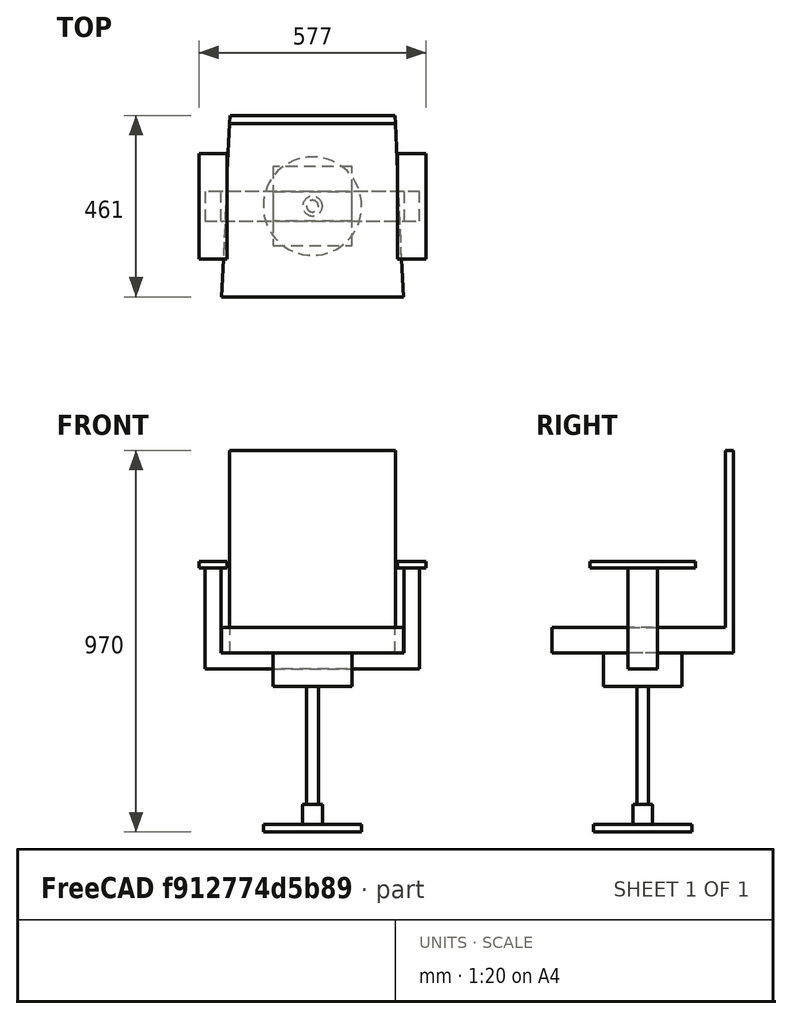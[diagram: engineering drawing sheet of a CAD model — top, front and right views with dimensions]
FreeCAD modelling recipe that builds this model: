
FCSTD DOCUMENT  (FreeCAD 1.0R39109 (Git))
Label: chair02_00503
License: All rights reserved
LicenseURL: https://en.wikipedia.org/wiki/All_rights_reserved
objects: TechDraw::DrawViewDimension×13, Sketcher::SketchObject×10, PartDesign::Pad×10, TechDraw::DrawViewAnnotation×9, PartDesign::Body×5, PartDesign::ShapeBinder×4, TechDraw::DrawSVGTemplate×3, TechDraw::DrawProjGroupItem×3, TechDraw::DrawPage×3, TechDraw::DrawViewSection×3, App::Part×1
note: 85 computed .brp shape members not serialized (recipe doc carries the construction recipe); baked Part::Feature solids carry a one-line shape summary decoded from their .brp

FEATURE [Sketcher::SketchObject] Sketch
  ArcFitTolerance = 1e-06
  AttachmentSupport = -> [XY_Plane]
  FullyConstrained = true
  MakeInternals = false
  MapMode = 5
  sketch-geometry (1):
    g0: Circle CenterX=0 CenterY=0 CenterZ=0 NormalX=0 NormalY=0 NormalZ=1 AngleXU=0 Radius=125
  constraints (2):
    c: Diameter(g0) = 250
    c: Coincident(g0,g-1)
FEATURE [PartDesign::Pad] Pad
  Direction = (0,0,1)
  Length = 20
  Length2 = 10
  Profile = -> Sketch
  ReferenceAxis = -> Sketch [N_Axis]
  Refine = true
  Suppressed = false
  Type = 0
FEATURE [Sketcher::SketchObject] Sketch001
  ArcFitTolerance = 1e-06
  AttachmentSupport = -> [Pad]
  FullyConstrained = true
  MakeInternals = false
  MapMode = 5
  Placement = pos=(0,0,20) rot=(0,0,1;0rad)
  sketch-geometry (1):
    g0: Circle CenterX=0 CenterY=0 CenterZ=0 NormalX=0 NormalY=0 NormalZ=1 AngleXU=0 Radius=25
  constraints (2):
    c: Diameter(g0) = 50
    c: Coincident(g0,g-1)
FEATURE [PartDesign::Pad] Pad001
  BaseFeature = -> Pad
  Direction = (0,0,1)
  Length = 50
  Length2 = 10
  Profile = -> Sketch001
  ReferenceAxis = -> Sketch001 [N_Axis]
  Refine = true
  Suppressed = false
  Type = 0
FEATURE [PartDesign::Body] Body  label="Body1"
  AllowCompound = false
  Group = -> [Sketch,Pad,Sketch001,Pad001]
  Origin = -> Origin
  Tip = -> Pad001
FEATURE [PartDesign::ShapeBinder] CopyPad001  label="Body2_Sketch_P.lane"
  Placement = pos=(0,0,50) rot=(0,0,1;0rad)
  TraceSupport = false
FEATURE [Sketcher::SketchObject] Sketch002
  ArcFitTolerance = 1e-06
  AttachmentSupport = -> [CopyPad001]
  FullyConstrained = true
  MakeInternals = false
  MapMode = 5
  Placement = pos=(0,0,70) rot=(0,0,1;0rad)
  sketch-geometry (1):
    g0: Circle CenterX=0 CenterY=0 CenterZ=0 NormalX=0 NormalY=0 NormalZ=1 AngleXU=0 Radius=15
  constraints (2):
    c: Diameter(g0) = 30
    c: Coincident(g0,g-1)
FEATURE [PartDesign::Pad] Pad002
  Direction = (0,0,1)
  Length = 300
  Length2 = 10
  Placement = pos=(0,0,50) rot=(0,0,1;0rad)
  Profile = -> Sketch002
  ReferenceAxis = -> Sketch002 [N_Axis]
  Refine = true
  Suppressed = false
  Type = 0
FEATURE [PartDesign::Body] Body001  label="Body2"
  AllowCompound = false
  Group = -> [CopyPad001,Sketch002,Pad002]
  Origin = -> Origin001
  Tip = -> Pad002
FEATURE [PartDesign::ShapeBinder] CopyPad002  label="Body3_Sketch_Plane"
  Placement = pos=(0,0,300) rot=(0,0,1;0rad)
  TraceSupport = false
FEATURE [Sketcher::SketchObject] Sketch003
  ArcFitTolerance = 1e-06
  AttachmentSupport = -> [CopyPad002]
  FullyConstrained = true
  MakeInternals = false
  MapMode = 5
  Placement = pos=(0,0,370) rot=(0,0,1;0rad)
  sketch-geometry (5):
    g0: LineSegment StartX=-100 StartY=-100 StartZ=0 EndX=100 EndY=-100 EndZ=0
    g1: LineSegment StartX=100 StartY=-100 StartZ=0 EndX=100 EndY=100 EndZ=0
    g2: LineSegment StartX=100 StartY=100 StartZ=0 EndX=-100 EndY=100 EndZ=0
    g3: LineSegment StartX=-100 StartY=100 StartZ=0 EndX=-100 EndY=-100 EndZ=0
    g4: GeomPoint [constr] X=0 Y=0 Z=0
  constraints (12):
    c: Coincident(g0,g1)
    c: Coincident(g1,g2)
    c: Coincident(g2,g3)
    c: Coincident(g3,g0)
    c: Horizontal(g0)
    c: Horizontal(g2)
    c: Vertical(g1)
    c: Vertical(g3)
    c: Symmetric(g2,g0,g4)
    c: Distance(g1,g3) = 200
    c: Distance(g0,g2) = 200
    c: Coincident(g4,g-1)
FEATURE [PartDesign::Pad] Pad003
  Direction = (0,0,1)
  Length = 45
  Length2 = 10
  Placement = pos=(0,0,300) rot=(0,0,1;0rad)
  Profile = -> Sketch003
  ReferenceAxis = -> Sketch003 [N_Axis]
  Refine = true
  Suppressed = false
  Type = 0
FEATURE [PartDesign::ShapeBinder] CopyPad003  label="Body4_Sketch_Plane"
  Placement = pos=(0,0,45) rot=(0,0,1;0rad)
  TraceSupport = false
FEATURE [Sketcher::SketchObject] Sketch004
  ArcFitTolerance = 1e-06
  AttachmentSupport = -> [CopyPad003]
  FullyConstrained = true
  MakeInternals = false
  MapMode = 5
  Placement = pos=(0,0,415) rot=(0,0,1;0rad)
  sketch-geometry (5):
    g0: LineSegment StartX=-272.5 StartY=-37.5 StartZ=0 EndX=272.5 EndY=-37.5 EndZ=0
    g1: LineSegment StartX=272.5 StartY=-37.5 StartZ=0 EndX=272.5 EndY=37.5 EndZ=0
    g2: LineSegment StartX=272.5 StartY=37.5 StartZ=0 EndX=-272.5 EndY=37.5 EndZ=0
    g3: LineSegment StartX=-272.5 StartY=37.5 StartZ=0 EndX=-272.5 EndY=-37.5 EndZ=0
    g4: GeomPoint [constr] X=0 Y=0 Z=0
  constraints (12):
    c: Coincident(g0,g1)
    c: Coincident(g1,g2)
    c: Coincident(g2,g3)
    c: Coincident(g3,g0)
    c: Horizontal(g0)
    c: Horizontal(g2)
    c: Vertical(g1)
    c: Vertical(g3)
    c: Symmetric(g2,g0,g4)
    c: Distance(g1,g3) = 545
    c: Distance(g0,g2) = 75
    c: Coincident(g4,g-1)
FEATURE [PartDesign::Pad] Pad004
  Direction = (0,0,1)
  Length = 40
  Length2 = 10
  Placement = pos=(0,0,45) rot=(0,0,1;0rad)
  Profile = -> Sketch004
  ReferenceAxis = -> Sketch004 [N_Axis]
  Refine = true
  Suppressed = false
  Type = 0
FEATURE [Sketcher::SketchObject] Sketch005
  ArcFitTolerance = 1e-06
  AttachmentSupport = -> [Pad004]
  ExternalGeometry = -> [Pad004]
  FullyConstrained = true
  MakeInternals = false
  MapMode = 5
  Placement = pos=(0,0,455) rot=(0,0,1;0rad)
  sketch-geometry (8):
    g0: LineSegment StartX=-272.5 StartY=37.5 StartZ=0 EndX=-272.5 EndY=-37.5 EndZ=0
    g1: LineSegment StartX=-272.5 StartY=-37.5 StartZ=0 EndX=-232.5 EndY=-37.5 EndZ=0
    g2: LineSegment StartX=-232.5 StartY=-37.5 StartZ=0 EndX=-232.5 EndY=37.5 EndZ=0
    g3: LineSegment StartX=-232.5 StartY=37.5 StartZ=0 EndX=-272.5 EndY=37.5 EndZ=0
    g4: LineSegment StartX=272.5 StartY=37.5 StartZ=0 EndX=232.5 EndY=37.5 EndZ=0
    g5: LineSegment StartX=232.5 StartY=37.5 StartZ=0 EndX=232.5 EndY=-37.5 EndZ=0
    g6: LineSegment StartX=232.5 StartY=-37.5 StartZ=0 EndX=272.5 EndY=-37.5 EndZ=0
    g7: LineSegment StartX=272.5 StartY=-37.5 StartZ=0 EndX=272.5 EndY=37.5 EndZ=0
  constraints (22):
    c: Coincident(g0,g1)
    c: Coincident(g1,g2)
    c: Coincident(g2,g3)
    c: Coincident(g3,g0)
    c: Vertical(g0)
    c: Vertical(g2)
    c: Horizontal(g1)
    c: Horizontal(g3)
    c: Coincident(g0,g-3)
    c: PointOnObject(g1,g-4)
    c: DistanceX(g3,g3) = 40
    c: Coincident(g4,g5)
    c: Coincident(g5,g6)
    c: Coincident(g6,g7)
    c: Coincident(g7,g4)
    c: Horizontal(g4)
    c: Horizontal(g6)
    c: Vertical(g5)
    c: Vertical(g7)
    c: Coincident(g4,g-3)
    c: PointOnObject(g5,g-4)
    c: Equal(g4,g3)
FEATURE [PartDesign::Pad] Pad005
  BaseFeature = -> Pad004
  Direction = (0,0,1)
  Length = 216
  Length2 = 10
  Placement = pos=(0,0,45) rot=(0,0,1;0rad)
  Profile = -> Sketch005
  ReferenceAxis = -> Sketch005 [N_Axis]
  Refine = true
  Suppressed = false
  Type = 0
FEATURE [Sketcher::SketchObject] Sketch006
  ArcFitTolerance = 1e-06
  AttachmentSupport = -> [Pad005]
  ExternalGeometry = -> [Pad005]
  FullyConstrained = true
  MakeInternals = false
  MapMode = 5
  Placement = pos=(0,0,671) rot=(0,0,1;0rad)
  sketch-geometry (16):
    g0: LineSegment StartX=-288.5 StartY=134 StartZ=0 EndX=-288.5 EndY=-134 EndZ=0
    g1: LineSegment StartX=-288.5 StartY=-134 StartZ=0 EndX=-216.5 EndY=-134 EndZ=0
    g2: LineSegment StartX=-216.5 StartY=-134 StartZ=0 EndX=-216.5 EndY=134 EndZ=0
    g3: LineSegment StartX=-216.5 StartY=134 StartZ=0 EndX=-288.5 EndY=134 EndZ=0
    g4: LineSegment StartX=216.5 StartY=134 StartZ=0 EndX=216.5 EndY=-134 EndZ=0
    g5: LineSegment StartX=216.5 StartY=-134 StartZ=0 EndX=288.5 EndY=-134 EndZ=0
    g6: LineSegment StartX=288.5 StartY=-134 StartZ=0 EndX=288.5 EndY=134 EndZ=0
    g7: LineSegment StartX=288.5 StartY=134 StartZ=0 EndX=216.5 EndY=134 EndZ=0
    g8: LineSegment [constr] StartX=-272.5 StartY=37.5 StartZ=0 EndX=-232.5 EndY=-37.5 EndZ=0
    g9: LineSegment [constr] StartX=-252.5 StartY=0 StartZ=0 EndX=-272.5 EndY=-37.5 EndZ=0
    g10: LineSegment [constr] StartX=232.5 StartY=37.5 StartZ=0 EndX=272.5 EndY=-37.5 EndZ=0
    g11: LineSegment [constr] StartX=272.5 StartY=37.5 StartZ=0 EndX=252.5 EndY=0 EndZ=0
    g12: LineSegment [constr] StartX=-216.5 StartY=134 StartZ=0 EndX=-288.5 EndY=-134 EndZ=0
    g13: LineSegment [constr] StartX=-288.5 StartY=134 StartZ=0 EndX=-252.5 EndY=0 EndZ=0
    g14: LineSegment [constr] StartX=216.5 StartY=134 StartZ=0 EndX=288.5 EndY=-134 EndZ=0
    g15: LineSegment [constr] StartX=288.5 StartY=134 StartZ=0 EndX=252.5 EndY=0 EndZ=0
  constraints (38):
    c: Coincident(g0,g1)
    c: Coincident(g1,g2)
    c: Coincident(g2,g3)
    c: Coincident(g3,g0)
    c: Vertical(g0)
    c: Vertical(g2)
    c: Horizontal(g1)
    c: Horizontal(g3)
    c: Coincident(g4,g5)
    c: Coincident(g5,g6)
    c: Coincident(g6,g7)
    c: Coincident(g7,g4)
    c: Vertical(g4)
    c: Vertical(g6)
    c: Horizontal(g5)
    c: Horizontal(g7)
    c: Equal(g7,g3)
    c: Equal(g2,g4)
    c: DistanceX(g3,g3) = 72
    c: Coincident(g8,g-4)
    c: Coincident(g8,g-3)
    c: Coincident(g9,g-4)
    c: Coincident(g10,g-5)
    c: Coincident(g10,g-6)
    c: Coincident(g11,g-6)
    c: Symmetric(g10,g10,g11)
    c: Symmetric(g8,g8,g9)
    c: Coincident(g12,g2)
    c: Coincident(g12,g0)
    c: Coincident(g13,g0)
    c: Symmetric(g12,g12,g13)
    c: Coincident(g9,g13)
    c: Coincident(g14,g4)
    c: Coincident(g14,g5)
    c: Coincident(g15,g6)
    c: Symmetric(g14,g14,g15)
    c: Coincident(g15,g11)
    c: DistanceY(g2,g2) = 268
FEATURE [PartDesign::Pad] Pad006
  BaseFeature = -> Pad005
  Direction = (0,0,1)
  Length = 17
  Length2 = 10
  Placement = pos=(0,0,45) rot=(0,0,1;0rad)
  Profile = -> Sketch006
  ReferenceAxis = -> Sketch006 [N_Axis]
  Refine = true
  Suppressed = false
  Type = 0
FEATURE [PartDesign::Body] Body003  label="Body4"
  AllowCompound = false
  Group = -> [CopyPad003,Sketch004,Pad004,Sketch005,Pad005,Sketch006,Pad006]
  Origin = -> Origin003
  Tip = -> Pad006
FEATURE [PartDesign::ShapeBinder] CopyPad006  label="Body5_Sketch_Plane"
  Placement = pos=(0,0,45) rot=(0,0,1;0rad)
  TraceSupport = false
FEATURE [Sketcher::SketchObject] Sketch009
  ArcFitTolerance = 1e-06
  AttachmentSupport = -> [Pad003]
  ExternalGeometry = -> [Pad003]
  FullyConstrained = true
  MakeInternals = false
  MapMode = 5
  Placement = pos=(0,0,415) rot=(0,0,1;0rad)
  sketch-geometry (8):
    g0: LineSegment StartX=-100 StartY=100 StartZ=0 EndX=-100 EndY=37.5 EndZ=0
    g1: LineSegment StartX=-100 StartY=37.5 StartZ=0 EndX=100 EndY=37.5 EndZ=0
    g2: LineSegment StartX=100 StartY=37.5 StartZ=0 EndX=100 EndY=100 EndZ=0
    g3: LineSegment StartX=100 StartY=100 StartZ=0 EndX=-100 EndY=100 EndZ=0
    g4: LineSegment StartX=100 StartY=-100 StartZ=0 EndX=100 EndY=-37.5 EndZ=0
    g5: LineSegment StartX=100 StartY=-37.5 StartZ=0 EndX=-100 EndY=-37.5 EndZ=0
    g6: LineSegment StartX=-100 StartY=-37.5 StartZ=0 EndX=-100 EndY=-100 EndZ=0
    g7: LineSegment StartX=-100 StartY=-100 StartZ=0 EndX=100 EndY=-100 EndZ=0
  constraints (21):
    c: Coincident(g0,g1)
    c: Coincident(g1,g2)
    c: Coincident(g2,g3)
    c: Coincident(g3,g0)
    c: Vertical(g0)
    c: Vertical(g2)
    c: Horizontal(g1)
    c: Horizontal(g3)
    c: Coincident(g0,g-3)
    c: PointOnObject(g1,g-4)
    c: Coincident(g4,g5)
    c: Coincident(g5,g6)
    c: Coincident(g6,g7)
    c: Coincident(g7,g4)
    c: Vertical(g6)
    c: Horizontal(g5)
    c: Horizontal(g7)
    c: Coincident(g4,g-4)
    c: PointOnObject(g5,g-3)
    c: DistanceY(g4,g1) = 75
    c: Symmetric(g1,g4,g-1)
FEATURE [PartDesign::Pad] Pad009
  BaseFeature = -> Pad003
  Direction = (0,0,1)
  Length = 40
  Length2 = 10
  Placement = pos=(0,0,300) rot=(0,0,1;0rad)
  Profile = -> Sketch009
  ReferenceAxis = -> Sketch009 [N_Axis]
  Refine = true
  Suppressed = false
  Type = 0
FEATURE [PartDesign::Body] Body002  label="Body3"
  AllowCompound = false
  Group = -> [CopyPad002,Sketch003,Pad003,Sketch009,Pad009]
  Origin = -> Origin002
  Tip = -> Pad009
FEATURE [Sketcher::SketchObject] Sketch007
  ArcFitTolerance = 1e-06
  AttachmentSupport = -> [CopyPad006]
  FullyConstrained = true
  MakeInternals = false
  MapMode = 5
  Placement = pos=(0,0,455) rot=(0,0,1;0rad)
  sketch-geometry (8):
    g0: LineSegment StartX=-210 StartY=230.5 StartZ=0 EndX=-231 EndY=-230.5 EndZ=0
    g1: LineSegment StartX=-231 StartY=-230.5 StartZ=0 EndX=231 EndY=-230.5 EndZ=0
    g2: LineSegment StartX=231 StartY=-230.5 StartZ=0 EndX=210 EndY=230.5 EndZ=0
    g3: LineSegment StartX=210 StartY=230.5 StartZ=0 EndX=-210 EndY=230.5 EndZ=0
    g4: LineSegment [constr] StartX=210 StartY=230.5 StartZ=0 EndX=2.84e-14 EndY=0 EndZ=0
    g5: LineSegment [constr] StartX=2.84e-14 StartY=0 StartZ=0 EndX=-210 EndY=230.5 EndZ=0
    g6: LineSegment [constr] StartX=210 StartY=230.5 StartZ=0 EndX=210 EndY=0 EndZ=0
    g7: LineSegment [constr] StartX=231 StartY=-230.5 StartZ=0 EndX=231 EndY=0 EndZ=0
  constraints (20):
    c: Coincident(g2,g1)
    c: DistanceX(g1,g1) = 462
    c: DistanceX(g3,g3) = 420
    c: Coincident(g1,g0)
    c: Symmetric(g2,g0,g-2)
    c: Coincident(g2,g3)
    c: Coincident(g3,g0)
    c: Coincident(g4,g2)
    c: Coincident(g4,g-1)
    c: Coincident(g5,g4)
    c: Coincident(g5,g0)
    c: DistanceY(g2,g2) = 461
    c: Coincident(g6,g2)
    c: PointOnObject(g6,g-1)
    c: Vertical(g6)
    c: Coincident(g7,g1)
    c: PointOnObject(g7,g-1)
    c: Vertical(g7)
    c: Equal(g7,g6)
    c: Symmetric(g1,g0,g-2)
FEATURE [PartDesign::Pad] Pad007
  Direction = (0,0,1)
  Length = 65
  Length2 = 10
  Placement = pos=(0,0,45) rot=(0,0,1;0rad)
  Profile = -> Sketch007
  ReferenceAxis = -> Sketch007 [N_Axis]
  Refine = true
  Suppressed = false
  Type = 0
FEATURE [Sketcher::SketchObject] Sketch008
  ArcFitTolerance = 1e-06
  AttachmentSupport = -> [Pad007]
  ExternalGeometry = -> [Pad007]
  FullyConstrained = true
  MakeInternals = false
  MapMode = 5
  Placement = pos=(0,0,520) rot=(0,0,1;0rad)
  sketch-geometry (4):
    g0: LineSegment StartX=-210 StartY=230.5 StartZ=0 EndX=210 EndY=230.5 EndZ=0
    g1: LineSegment StartX=-210 StartY=230.5 StartZ=0 EndX=-210.957 EndY=209.5 EndZ=0
    g2: LineSegment StartX=-210.957 StartY=209.5 StartZ=0 EndX=210.957 EndY=209.5 EndZ=0
    g3: LineSegment StartX=210 StartY=230.5 StartZ=0 EndX=210.957 EndY=209.5 EndZ=0
  constraints (10):
    c: Coincident(g0,g-3)
    c: Coincident(g0,g-4)
    c: Coincident(g1,g0)
    c: PointOnObject(g1,g-3)
    c: Coincident(g2,g1)
    c: PointOnObject(g2,g-4)
    c: Horizontal(g2)
    c: Coincident(g3,g0)
    c: Coincident(g3,g2)
    c: DistanceY(g1,g1) = 21
FEATURE [PartDesign::Pad] Pad008
  BaseFeature = -> Pad007
  Direction = (0,0,1)
  Length = 450
  Length2 = 10
  Placement = pos=(0,0,45) rot=(0,0,1;0rad)
  Profile = -> Sketch008
  ReferenceAxis = -> Sketch008 [N_Axis]
  Refine = true
  Suppressed = false
  Type = 0
FEATURE [PartDesign::Body] Body004  label="Body5"
  AllowCompound = false
  Group = -> [CopyPad006,Sketch007,Pad007,Sketch008,Pad008]
  Origin = -> Origin004
  Tip = -> Pad008
FEATURE [App::Part] Part  label="chair02"
  Group = -> [Body,Body001,Body002,Body003,Body004]
  Origin = -> Origin005
FEATURE [TechDraw::DrawSVGTemplate] Template  label="テンプレート"
  Height = 210
  Orientation = 1
  Template = <userpath>/AppData/Local/Programs/FreeCAD 1.0/data/Mod/TechDraw/Templates/A4_Landscape_blank.svg
  Width = 297
FEATURE [TechDraw::DrawProjGroupItem] View
  CoarseView = false
  Direction = (0,0,1)
  Focus = 100
  HardHidden = true
  IsoCount = 0
  IsoHidden = false
  IsoVisible = false
  LockPosition = false
  Perspective = false
  Rotation = 0
  RotationVector = (1,0,0)
  Scale = 0.333333
  ScaleType = 2
  ScrubCount = 1
  SeamHidden = false
  SeamVisible = false
  SmoothHidden = false
  SmoothVisible = true
  Source = -> [Part]
  Type = 0
  X = 131.425
  XDirection = (1,0,0)
  Y = 107.897
FEATURE [TechDraw::DrawViewDimension] Dimension  label="寸法"
  AngleOverride = false
  Arbitrary = false
  ArbitraryTolerances = false
  BoxCorners = (2) [(-96.1666,-76.8333,0),(96.1666,76.8333,0)]
  EqualTolerance = true
  ExtensionAngle = 0
  FormatSpec = %.2w
  FormatSpecOverTolerance = %+.2w
  FormatSpecUnderTolerance = %+.2w
  Inverted = false
  LineAngle = 0
  LockPosition = false
  MeasureType = 1
  OverTolerance = 0
  References2D = -> [View]
  Rotation = 0
  Scale = 0.2
  ScaleType = 2
  TheoreticalExact = false
  Type = 1
  UnderTolerance = 0
  X = 0
  Y = 93.9298
FEATURE [TechDraw::DrawViewDimension] Dimension001  label="寸法001"
  AngleOverride = false
  Arbitrary = false
  ArbitraryTolerances = false
  BoxCorners = (2) [(-96.1666,-76.8333,0),(96.1666,76.8333,0)]
  EqualTolerance = true
  ExtensionAngle = 0
  FormatSpec = %.2w
  FormatSpecOverTolerance = %+.2w
  FormatSpecUnderTolerance = %+.2w
  Inverted = false
  LineAngle = 0
  LockPosition = false
  MeasureType = 1
  OverTolerance = 0
  References2D = -> [View]
  Rotation = 0
  Scale = 0.2
  ScaleType = 2
  TheoreticalExact = false
  Type = 2
  UnderTolerance = 0
  X = 135.701
  Y = 0
FEATURE [TechDraw::DrawViewDimension] Dimension002  label="寸法002"
  AngleOverride = false
  Arbitrary = false
  ArbitraryTolerances = false
  BoxCorners = (2) [(-96.1666,-76.8333,0),(96.1666,76.8333,0)]
  EqualTolerance = true
  ExtensionAngle = 0
  FormatSpec = %.2w
  FormatSpecOverTolerance = %+.2w
  FormatSpecUnderTolerance = %+.2w
  Inverted = false
  LineAngle = 0
  LockPosition = false
  MeasureType = 1
  OverTolerance = 0
  References2D = -> [View]
  Rotation = 0
  Scale = 0.2
  ScaleType = 2
  TheoreticalExact = false
  Type = 2
  UnderTolerance = 0
  X = 113.57
  Y = 61.6706
FEATURE [TechDraw::DrawViewDimension] Dimension003  label="寸法003"
  AngleOverride = false
  Arbitrary = false
  ArbitraryTolerances = false
  BoxCorners = (2) [(-96.1666,-76.8333,0),(96.1666,76.8333,0)]
  EqualTolerance = true
  ExtensionAngle = 0
  FormatSpec = %.2w
  FormatSpecOverTolerance = %+.2w
  FormatSpecUnderTolerance = %+.2w
  Inverted = false
  LineAngle = 0
  LockPosition = false
  MeasureType = 1
  OverTolerance = 0
  References2D = -> [View]
  Rotation = 0
  Scale = 0.2
  ScaleType = 2
  TheoreticalExact = false
  Type = 2
  UnderTolerance = 0
  X = 125.233
  Y = 0.063601
FEATURE [TechDraw::DrawViewDimension] Dimension004  label="寸法004"
  AngleOverride = false
  Arbitrary = false
  ArbitraryTolerances = false
  BoxCorners = (2) [(-96.1666,-76.8333,0),(96.1666,76.8333,0)]
  EqualTolerance = true
  ExtensionAngle = 0
  FormatSpec = %.2w
  FormatSpecOverTolerance = %+.2w
  FormatSpecUnderTolerance = %+.2w
  Inverted = false
  LineAngle = 0
  LockPosition = false
  MeasureType = 1
  OverTolerance = 0
  References2D = -> [View]
  Rotation = 0
  Scale = 0.2
  ScaleType = 2
  TheoreticalExact = false
  Type = 1
  UnderTolerance = 0
  X = -84.1666
  Y = 58.5053
FEATURE [TechDraw::DrawViewDimension] Dimension005  label="寸法005"
  AngleOverride = false
  Arbitrary = false
  ArbitraryTolerances = false
  BoxCorners = (2) [(-96.1666,-76.8333,0),(96.1666,76.8333,0)]
  EqualTolerance = true
  ExtensionAngle = 0
  FormatSpec = %.2w
  FormatSpecOverTolerance = %+.2w
  FormatSpecUnderTolerance = %+.2w
  Inverted = false
  LineAngle = 0
  LockPosition = false
  MeasureType = 1
  OverTolerance = 0
  References2D = -> [View]
  Rotation = 0
  Scale = 0.2
  ScaleType = 2
  TheoreticalExact = false
  Type = 2
  UnderTolerance = 0
  X = -108.801
  Y = 0
FEATURE [TechDraw::DrawViewDimension] Dimension006  label="寸法006"
  AngleOverride = false
  Arbitrary = false
  ArbitraryTolerances = false
  BoxCorners = (2) [(-96.1666,-76.8333,0),(96.1666,76.8333,0)]
  EqualTolerance = true
  ExtensionAngle = 0
  FormatSpec = %.2w
  FormatSpecOverTolerance = %+.2w
  FormatSpecUnderTolerance = %+.2w
  Inverted = false
  LineAngle = 0
  LockPosition = false
  MeasureType = 1
  OverTolerance = 0
  References2D = -> [View]
  Rotation = 0
  Scale = 0.2
  ScaleType = 2
  TheoreticalExact = false
  Type = 1
  UnderTolerance = 0
  X = 0
  Y = -83.8244
FEATURE [TechDraw::DrawPage] Page  label="用紙"
  KeepUpdated = true
  NextBalloonIndex = 1
  ProjectionType = 0
  Template = -> Template
  Views = -> [View,Dimension,Dimension001,Dimension002,Dimension003,Dimension004,Dimension005,Dimension006]
FEATURE [TechDraw::DrawSVGTemplate] Template001  label="テンプレート001"
  Height = 210
  Orientation = 1
  Template = <userpath>/AppData/Local/Programs/FreeCAD 1.0/data/Mod/TechDraw/Templates/A4_Landscape_blank.svg
  Width = 297
FEATURE [TechDraw::DrawSVGTemplate] Template002  label="テンプレート002"
  Height = 210
  Orientation = 1
  Template = <userpath>/AppData/Local/Programs/FreeCAD 1.0/data/Mod/TechDraw/Templates/A4_Landscape_blank.svg
  Width = 297
FEATURE [TechDraw::DrawProjGroupItem] View001
  CoarseView = false
  Direction = (0,-1,0)
  Focus = 100
  HardHidden = true
  IsoCount = 0
  IsoHidden = false
  IsoVisible = false
  LockPosition = false
  Perspective = false
  Rotation = 0
  RotationVector = (1,0,0)
  Scale = 0.2
  ScaleType = 2
  ScrubCount = 1
  SeamHidden = false
  SeamVisible = false
  SmoothHidden = false
  SmoothVisible = true
  Source = -> [Part]
  Type = 0
  X = 72.2264
  XDirection = (1,0,0)
  Y = 108.632
FEATURE [TechDraw::DrawViewSection] SectionView  label="セクション  - "
  BaseView = -> View001
  CoarseView = false
  CutSurfaceDisplay = 2
  Direction = (1e-16,0,1)
  FileGeomPattern = <userpath>\AppData\Local\Programs\FreeCAD 1.0\data\Mod/TechDraw/PAT/FCPAT.pat
  FileHatchPattern = <userpath>\AppData\Local\Programs\FreeCAD 1.0\data\Mod/TechDraw/Patterns/simple.svg
  Focus = 100
  FuseBeforeCut = false
  HardHidden = true
  HatchOffset = (0,0,0)
  HatchRotation = 0
  HatchScale = 1
  IsoCount = 0
  IsoHidden = false
  IsoVisible = false
  LockPosition = false
  NameGeomPattern = Diamond
  Perspective = false
  Rotation = 0
  Scale = 0.15
  ScaleType = 2
  ScrubCount = 1
  SeamHidden = false
  SeamVisible = false
  SectionDirection = 4
  SectionLineStretch = 1
  SectionNormal = (1e-16,0,1)
  SectionOrigin = (0,0,581)
  SmoothHidden = false
  SmoothVisible = true
  Source = -> [Part]
  TrimAfterCut = false
  UsePreviousCut = false
  X = 215.858
  XDirection = (1,0,-1e-16)
  Y = 166.085
FEATURE [TechDraw::DrawViewSection] SectionView001  label="セクション001  - "
  BaseView = -> View001
  CoarseView = false
  CutSurfaceDisplay = 2
  Direction = (1e-16,0,1)
  FileGeomPattern = <userpath>\AppData\Local\Programs\FreeCAD 1.0\data\Mod/TechDraw/PAT/FCPAT.pat
  FileHatchPattern = <userpath>\AppData\Local\Programs\FreeCAD 1.0\data\Mod/TechDraw/Patterns/simple.svg
  Focus = 100
  FuseBeforeCut = false
  HardHidden = true
  HatchOffset = (0,0,0)
  HatchRotation = 0
  HatchScale = 1
  IsoCount = 0
  IsoHidden = false
  IsoVisible = false
  LockPosition = false
  NameGeomPattern = Diamond
  Perspective = false
  Rotation = 0
  Scale = 0.15
  ScaleType = 2
  ScrubCount = 1
  SeamHidden = false
  SeamVisible = false
  SectionDirection = 4
  SectionLineStretch = 1
  SectionNormal = (1e-16,0,1)
  SectionOrigin = (0,0,437)
  SmoothHidden = false
  SmoothVisible = true
  Source = -> [Part]
  TrimAfterCut = false
  UsePreviousCut = false
  X = 215.086
  XDirection = (1,0,-1e-16)
  Y = 92.3168
FEATURE [TechDraw::DrawViewSection] SectionView002  label="セクション002  - "
  BaseView = -> View001
  CoarseView = false
  CutSurfaceDisplay = 2
  Direction = (1e-16,0,1)
  FileGeomPattern = <userpath>\AppData\Local\Programs\FreeCAD 1.0\data\Mod/TechDraw/PAT/FCPAT.pat
  FileHatchPattern = <userpath>\AppData\Local\Programs\FreeCAD 1.0\data\Mod/TechDraw/Patterns/simple.svg
  Focus = 100
  FuseBeforeCut = false
  HardHidden = true
  HatchOffset = (0,0,0)
  HatchRotation = 0
  HatchScale = 1
  IsoCount = 0
  IsoHidden = false
  IsoVisible = false
  LockPosition = false
  NameGeomPattern = Diamond
  Perspective = false
  Rotation = 0
  Scale = 0.15
  ScaleType = 2
  ScrubCount = 1
  SeamHidden = false
  SeamVisible = false
  SectionDirection = 4
  SectionLineStretch = 1
  SectionNormal = (1e-16,0,1)
  SectionOrigin = (0,0,200)
  SmoothHidden = false
  SmoothVisible = true
  Source = -> [Part]
  TrimAfterCut = false
  UsePreviousCut = false
  X = 214.868
  XDirection = (1,0,-1e-16)
  Y = 24.434
FEATURE [TechDraw::DrawViewDimension] Dimension010  label="寸法010"
  AngleOverride = false
  Arbitrary = false
  ArbitraryTolerances = false
  BoxCorners = (2) [(-40.875,-18.75,0),(40.875,18.75,0)]
  EqualTolerance = true
  ExtensionAngle = 0
  FormatSpec = %.2w
  FormatSpecOverTolerance = %+.2w
  FormatSpecUnderTolerance = %+.2w
  Inverted = false
  LineAngle = 0
  LockPosition = false
  MeasureType = 1
  OverTolerance = 0
  References2D = -> [SectionView001]
  Rotation = 0
  Scale = 0.2
  ScaleType = 2
  TheoreticalExact = false
  Type = 1
  UnderTolerance = 0
  X = -23.2227
  Y = -15.8558
FEATURE [TechDraw::DrawViewDimension] Dimension011  label="寸法011"
  AngleOverride = false
  Arbitrary = false
  ArbitraryTolerances = false
  BoxCorners = (2) [(-40.875,-18.75,0),(40.875,18.75,0)]
  EqualTolerance = true
  ExtensionAngle = 0
  FormatSpec = %.2w
  FormatSpecOverTolerance = %+.2w
  FormatSpecUnderTolerance = %+.2w
  Inverted = false
  LineAngle = 0
  LockPosition = false
  MeasureType = 1
  OverTolerance = 0
  References2D = -> [SectionView001]
  Rotation = 0
  Scale = 0.2
  ScaleType = 2
  TheoreticalExact = false
  Type = 2
  UnderTolerance = 0
  X = 58.5124
  Y = 0
FEATURE [TechDraw::DrawViewDimension] Dimension016  label="寸法016"
  AngleOverride = false
  Arbitrary = false
  ArbitraryTolerances = false
  BoxCorners = (2) [(-40.875,-34.575,0),(40.875,34.575,0)]
  EqualTolerance = true
  ExtensionAngle = 0
  FormatSpec = %.2w
  FormatSpecOverTolerance = %+.2w
  FormatSpecUnderTolerance = %+.2w
  Inverted = false
  LineAngle = 0
  LockPosition = false
  MeasureType = 1
  OverTolerance = 0
  References2D = -> [SectionView]
  Rotation = 0
  Scale = 0.2
  ScaleType = 2
  TheoreticalExact = false
  Type = 1
  UnderTolerance = 0
  X = 21.6748
  Y = -21.6209
FEATURE [TechDraw::DrawViewAnnotation] Annotation  label="注釈"
  Font = osifont
  LineSpace = 100
  LockPosition = false
  MaxWidth = -1
  Rotation = 0
  Scale = 0.2
  ScaleType = 2
  Text = A
  TextSize = 5
  TextStyle = 0
  X = 143.937
  Y = 118.99
FEATURE [TechDraw::DrawViewAnnotation] Annotation001  label="注釈001"
  Font = osifont
  LineSpace = 100
  LockPosition = false
  MaxWidth = -1
  Rotation = 0
  Scale = 0.2
  ScaleType = 2
  Text = A
  TextSize = 5
  TextStyle = 0
  X = 9.25009
  Y = 118.99
FEATURE [TechDraw::DrawViewAnnotation] Annotation002  label="注釈002"
  Font = osifont
  LineSpace = 100
  LockPosition = false
  MaxWidth = -1
  Rotation = 0
  Scale = 0.2
  ScaleType = 2
  Text = B
  TextSize = 5
  TextStyle = 0
  X = 9.25009
  Y = 89.4351
FEATURE [TechDraw::DrawViewAnnotation] Annotation003  label="注釈003"
  Font = osifont
  LineSpace = 100
  LockPosition = false
  MaxWidth = -1
  Rotation = 0
  Scale = 0.2
  ScaleType = 2
  Text = B
  TextSize = 5
  TextStyle = 0
  X = 145.458
  Y = 89.4351
FEATURE [TechDraw::DrawViewAnnotation] Annotation004  label="注釈004"
  Font = osifont
  LineSpace = 100
  LockPosition = false
  MaxWidth = -1
  Rotation = 0
  Scale = 0.2
  ScaleType = 2
  Text = C
  TextSize = 5
  TextStyle = 0
  X = 145.458
  Y = 40.7495
FEATURE [TechDraw::DrawViewAnnotation] Annotation005  label="注釈005"
  Font = osifont
  LineSpace = 100
  LockPosition = false
  MaxWidth = -1
  Rotation = 0
  Scale = 0.2
  ScaleType = 2
  Text = C
  TextSize = 5
  TextStyle = 0
  X = 9.25009
  Y = 43.6474
FEATURE [TechDraw::DrawViewAnnotation] Annotation006  label="注釈006"
  Font = osifont
  LineSpace = 100
  LockPosition = false
  MaxWidth = -1
  Rotation = 0
  Scale = 0.2
  ScaleType = 2
  Text = A-A
  TextSize = 5
  TextStyle = 0
  X = 215.858
  Y = 205.891
FEATURE [TechDraw::DrawViewAnnotation] Annotation007  label="注釈007"
  Font = osifont
  LineSpace = 100
  LockPosition = false
  MaxWidth = -1
  Rotation = 0
  Scale = 0.2
  ScaleType = 2
  Text = B-B
  TextSize = 5
  TextStyle = 0
  X = 215.858
  Y = 117.871
FEATURE [TechDraw::DrawViewAnnotation] Annotation008  label="注釈008"
  Font = osifont
  LineSpace = 100
  LockPosition = false
  MaxWidth = -1
  Rotation = 0
  Scale = 0.2
  ScaleType = 2
  Text = C -C
  TextSize = 5
  TextStyle = 0
  X = 215.858
  Y = 48.4539
FEATURE [TechDraw::DrawProjGroupItem] View002
  CoarseView = false
  Direction = (0,-1,0)
  Focus = 100
  HardHidden = true
  IsoCount = 0
  IsoHidden = false
  IsoVisible = false
  LockPosition = false
  Perspective = false
  Rotation = 0
  RotationVector = (1,0,0)
  Scale = 0.2
  ScaleType = 2
  ScrubCount = 1
  SeamHidden = false
  SeamVisible = false
  SmoothHidden = false
  SmoothVisible = true
  Source = -> [Part]
  Type = 0
  X = 144.274
  XDirection = (1,0,0)
  Y = 104.736
FEATURE [TechDraw::DrawViewDimension] Dimension021  label="寸法021"
  AngleOverride = false
  Arbitrary = false
  ArbitraryTolerances = false
  BoxCorners = (2) [(-48.0834,-80.8335,-1e-07),(48.0834,80.8335,1e-07)]
  EqualTolerance = true
  ExtensionAngle = 0
  FormatSpec = %.2w
  FormatSpecOverTolerance = %+.2w
  FormatSpecUnderTolerance = %+.2w
  Inverted = false
  LineAngle = 0
  LockPosition = false
  MeasureType = 1
  OverTolerance = 0
  References2D = -> [View002]
  Rotation = 0
  Scale = 0.2
  ScaleType = 2
  TheoreticalExact = false
  Type = 2
  UnderTolerance = 0
  X = 64.6242
  Y = -30.3933
FEATURE [TechDraw::DrawViewDimension] Dimension029  label="寸法029"
  AngleOverride = false
  Arbitrary = false
  ArbitraryTolerances = false
  BoxCorners = (2) [(-48.0834,-80.8335,-1e-07),(48.0834,80.8335,1e-07)]
  EqualTolerance = true
  ExtensionAngle = 0
  FormatSpec = %.2w
  FormatSpecOverTolerance = %+.2w
  FormatSpecUnderTolerance = %+.2w
  Inverted = false
  LineAngle = 0
  LockPosition = false
  MeasureType = 1
  OverTolerance = 0
  References2D = -> [View002]
  Rotation = 0
  Scale = 0.2
  ScaleType = 2
  TheoreticalExact = false
  Type = 2
  UnderTolerance = 0
  X = -78.5928
  Y = 1.03446
FEATURE [TechDraw::DrawPage] Page001  label="用紙001"
  KeepUpdated = true
  NextBalloonIndex = 1
  ProjectionType = 0
  Template = -> Template001
  Views = -> [View002,Dimension021,Dimension029]
FEATURE [TechDraw::DrawViewDimension] Dimension012  label="寸法012"
  AngleOverride = false
  Arbitrary = false
  ArbitraryTolerances = false
  BoxCorners = (2) [(-40.875,-18.75,0),(40.875,18.75,0)]
  EqualTolerance = true
  ExtensionAngle = 0
  FormatSpec = %.2w
  FormatSpecOverTolerance = %+.2w
  FormatSpecUnderTolerance = %+.2w
  Inverted = false
  LineAngle = 0
  LockPosition = false
  MeasureType = 1
  OverTolerance = 0
  References2D = -> [SectionView001]
  Rotation = 0
  Scale = 0.2
  ScaleType = 2
  TheoreticalExact = false
  Type = 2
  UnderTolerance = 0
  X = 72.3404
  Y = 0
FEATURE [TechDraw::DrawPage] Page002  label="用紙002"
  KeepUpdated = true
  NextBalloonIndex = 1
  ProjectionType = 0
  Template = -> Template002
  Views = -> [View001,SectionView,SectionView001,SectionView002,Dimension010,Dimension011,Dimension016,Annotation,Annotation001,Annotation002,Annotation003,Annotation004,Annotation005,Annotation006,Annotation007,Annotation008,Dimension012]
